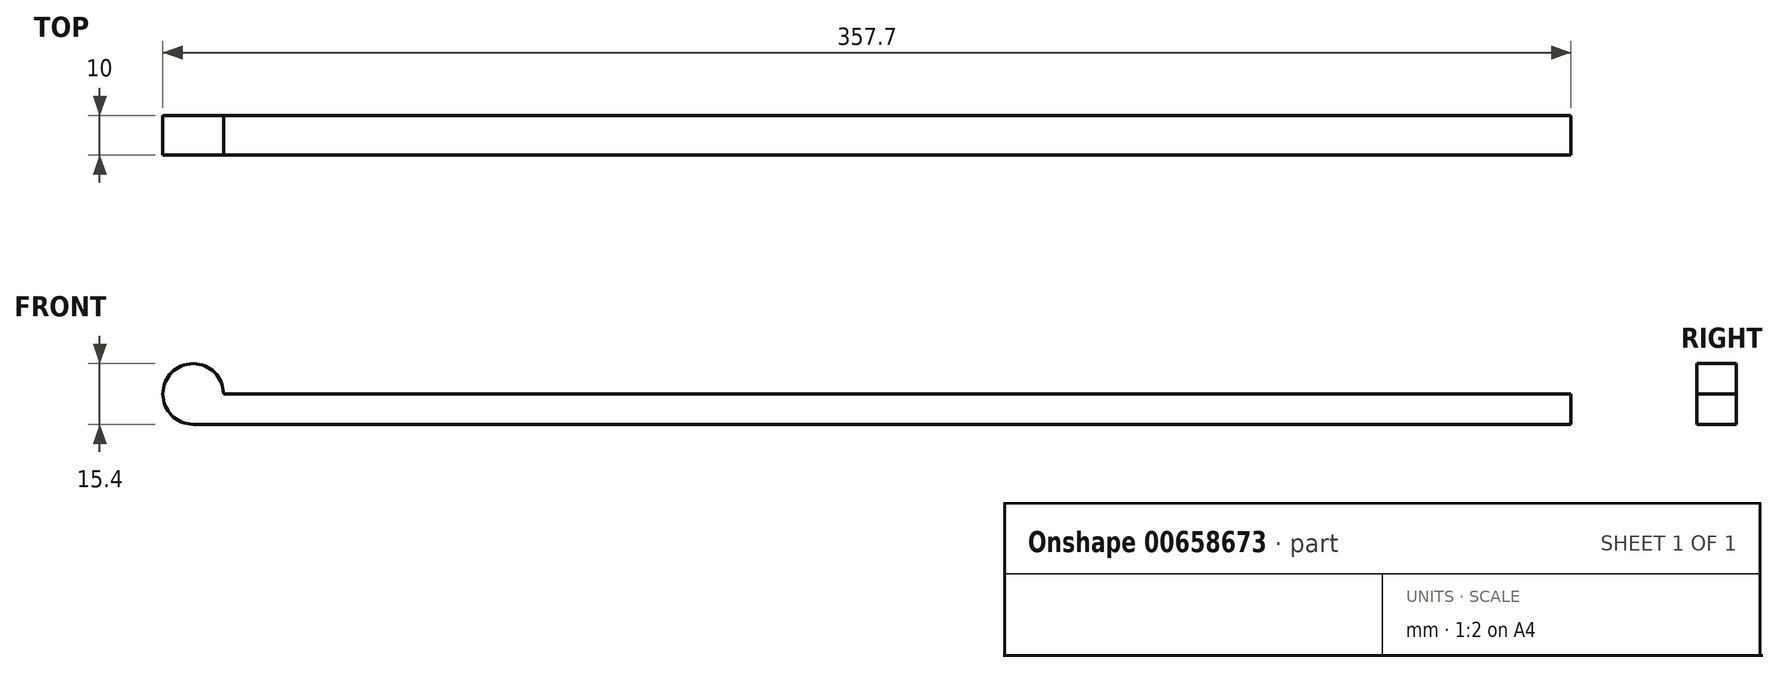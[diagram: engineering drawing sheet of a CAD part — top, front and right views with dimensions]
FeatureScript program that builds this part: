
annotation { "Feature Type Name" : "Feature", "Feature Type Description" : "" }
export const myFeature = defineFeature(function(context is Context, id is Id, definition is map)
    precondition{}
    {
        {
            var Q0;
            Q0=qCreatedBy(makeId("Front.planeOp"),FACE);
            var sketch = newSketch(context, id + "F0", { "sketchPlane" : qUnion([Q0])});
            skCircle(sketch, "E0", {"center": v(0, 0) * mm, "radius": 7.7 * mm});
            skLineSegment(sketch, "E1.bottom", {"start": v(0, 0) * mm, "end": v(350, 0) * mm});
            skLineSegment(sketch, "E1.top", {"start": v(0, -7.7) * mm, "end": v(350, -7.7) * mm});
            skLineSegment(sketch, "E1.left", {"start": v(0, 0) * mm, "end": v(0, -7.7) * mm});
            skLineSegment(sketch, "E1.right", {"start": v(350, 0) * mm, "end": v(350, -7.7) * mm});
            skSolve(sketch);
        }
        {
            var Q0;
            {var subQ0=sQuery(id+"F0.wireOp",EDGE,"E1.top");Q0=makeQuery(id+"F0.imprint","IMPRINT",FACE,{"disambiguationData":[TD([[makeQuery(id+"F0.imprint","IMPRINT",EDGE,{"derivedFrom":subQ0}),1.0]])]});}
            var Q1;
            {var subQ0=sQuery(id+"F0.wireOp",EDGE,"E1.left");Q1=makeQuery(id+"F0.imprint","IMPRINT",FACE,{"disambiguationData":[TD([[makeQuery(id+"F0.imprint","IMPRINT",EDGE,{"derivedFrom":subQ0}),-1.0]])]});}
            var Q2;
            {var subQ0=sQuery(id+"F0.wireOp",EDGE,"E1.left");Q2=makeQuery(id+"F0.imprint","IMPRINT",FACE,{"disambiguationData":[TD([[makeQuery(id+"F0.imprint","IMPRINT",EDGE,{"derivedFrom":subQ0}),1.0]])]});}
            extrude(context, id + "F1", {"entities" : qUnion([Q0, Q1, Q2]), "depth" : 10 * mm});
        }
    });
